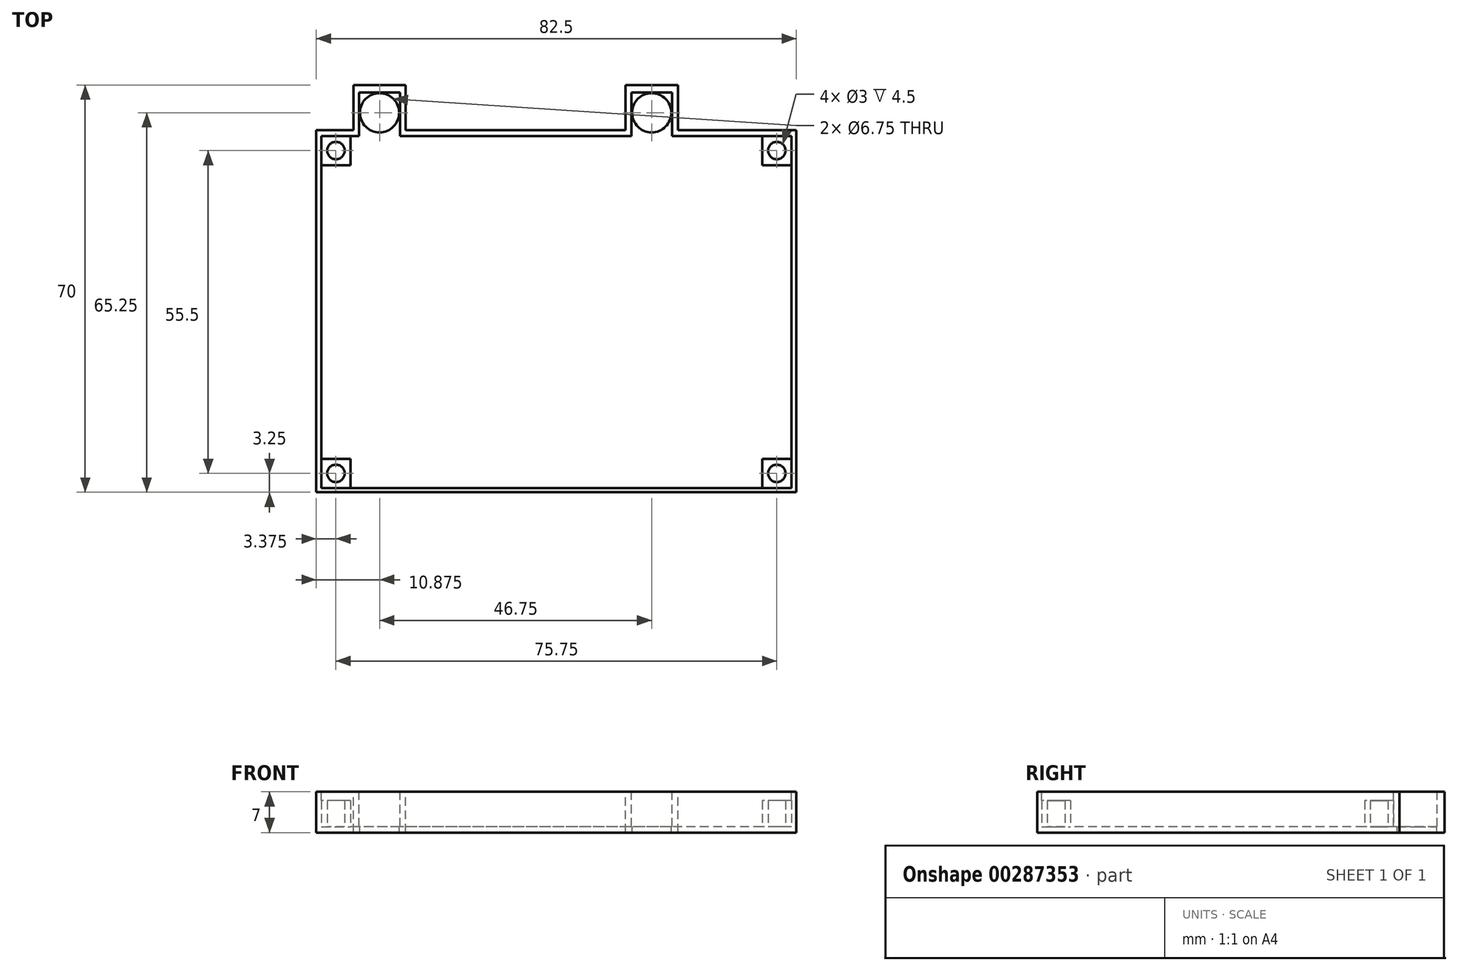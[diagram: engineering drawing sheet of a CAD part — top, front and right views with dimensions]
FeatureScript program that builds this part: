
annotation { "Feature Type Name" : "Feature", "Feature Type Description" : "" }
export const myFeature = defineFeature(function(context is Context, id is Id, definition is map)
    precondition{}
    {
        {
            var Q0;
            Q0=qCreatedBy(makeId("Top.planeOp"),FACE);
            var sketch = newSketch(context, id + "F0", { "sketchPlane" : qUnion([Q0])});
            skLineSegment(sketch, "E0.bottom", {"start": v(41.25, 35) * mm, "end": v(-41.25, 35) * mm});
            skLineSegment(sketch, "E0.top", {"start": v(41.25, -35) * mm, "end": v(-41.25, -35) * mm});
            skLineSegment(sketch, "E0.left", {"start": v(41.25, 35) * mm, "end": v(41.25, -35) * mm});
            skLineSegment(sketch, "E0.right", {"start": v(-41.25, 35) * mm, "end": v(-41.25, -35) * mm});
            skPoint(sketch, "E0.middle", {"position": v(0, 0) * mm});
            skSolve(sketch);
        }
        {
            var Q0;
            Q0=makeQuery(id+"F0.imprint","IMPRINT",FACE,{"disambiguationData":[TD([[makeQuery(id+"F0.imprint","IMPRINT",EDGE,{"derivedFrom":sQuery(id+"F0.wireOp",EDGE,"E0.bottom")}),1.0]])]});
            extrude(context, id + "F1", {"entities" : qUnion([Q0]), "depth" : 7 * mm});
        }
        {
            var Q0;
            Q0=makeQuery(id+"F1.opExtrude","CAP_FACE",FACE,{"disambiguationData":[OSD([sQuery(id+"F0.wireOp",EDGE,"E0.bottom"),sQuery(id+"F0.wireOp",EDGE,"E0.top"),sQuery(id+"F0.wireOp",EDGE,"E0.left"),sQuery(id+"F0.wireOp",EDGE,"E0.right")])],"isStart":false});
            var sketch = newSketch(context, id + "F2", { "sketchPlane" : qUnion([Q0])});
            skLineSegment(sketch, "E1.bottom", {"start": v(40.38, 26.25) * mm, "end": v(-40.38, 26.25) * mm});
            skLineSegment(sketch, "E1.top", {"start": v(40.38, -34.25) * mm, "end": v(-40.38, -34.25) * mm});
            skLineSegment(sketch, "E1.left", {"start": v(40.38, 26.25) * mm, "end": v(40.38, -34.25) * mm});
            skLineSegment(sketch, "E1.right", {"start": v(-40.38, 26.25) * mm, "end": v(-40.38, -34.25) * mm});
            skPoint(sketch, "E1.middle", {"position": v(0, -4) * mm});
            skLineSegment(sketch, "E2.bottom", {"start": v(-26.88, 33.75) * mm, "end": v(-33.88, 33.75) * mm});
            skLineSegment(sketch, "E2.top", {"start": v(-26.88, 26.25) * mm, "end": v(-33.88, 26.25) * mm});
            skLineSegment(sketch, "E2.left", {"start": v(-26.88, 33.75) * mm, "end": v(-26.88, 26.25) * mm});
            skLineSegment(sketch, "E2.right", {"start": v(-33.88, 33.75) * mm, "end": v(-33.88, 26.25) * mm});
            skPoint(sketch, "E2.middle", {"position": v(-30.38, 30) * mm});
            skLineSegment(sketch, "E3.bottom", {"start": v(19.87, 33.75) * mm, "end": v(12.87, 33.75) * mm});
            skLineSegment(sketch, "E3.top", {"start": v(19.87, 26.25) * mm, "end": v(12.87, 26.25) * mm});
            skLineSegment(sketch, "E3.left", {"start": v(19.87, 33.75) * mm, "end": v(19.87, 26.25) * mm});
            skLineSegment(sketch, "E3.right", {"start": v(12.87, 33.75) * mm, "end": v(12.87, 26.25) * mm});
            skPoint(sketch, "E3.middle", {"position": v(16.37, 30) * mm});
            skSolve(sketch);
        }
        {
            var Q0;
            Q0=makeQuery(id+"F2.imprint","IMPRINT",FACE,{"disambiguationData":[TD([[makeQuery(id+"F2.imprint","IMPRINT",EDGE,{"derivedFrom":sQuery(id+"F2.wireOp",EDGE,"E1.top")}),-1.0]])]});
            var Q1;
            Q1=makeQuery(id+"F2.imprint","IMPRINT",FACE,{"disambiguationData":[TD([[makeQuery(id+"F2.imprint","IMPRINT",EDGE,{"derivedFrom":sQuery(id+"F2.wireOp",EDGE,"E2.bottom")}),1.0]])]});
            var Q2;
            Q2=makeQuery(id+"F2.imprint","IMPRINT",FACE,{"disambiguationData":[TD([[makeQuery(id+"F2.imprint","IMPRINT",EDGE,{"derivedFrom":sQuery(id+"F2.wireOp",EDGE,"E3.bottom")}),1.0]])]});
            extrude(context, id + "F3", {"entities" : qUnion([Q0, Q1, Q2]), "operationType" : NewBodyOperationType.REMOVE, "oppositeDirection" : true, "depth" : 6 * mm});
        }
        {
            var Q0;
            Q0=makeQuery(id+"F3.boolean.opBoolean","COPY",FACE,{"derivedFrom":makeQuery(id+"F3.opExtrude","CAP_FACE",FACE,{"disambiguationData":[OSD([sQuery(id+"F2.wireOp",EDGE,"E1.bottom"),sQuery(id+"F2.wireOp",EDGE,"E1.top"),sQuery(id+"F2.wireOp",EDGE,"E1.left"),sQuery(id+"F2.wireOp",EDGE,"E1.right"),sQuery(id+"F2.wireOp",EDGE,"E2.bottom"),sQuery(id+"F2.wireOp",EDGE,"E2.left"),sQuery(id+"F2.wireOp",EDGE,"E2.right"),sQuery(id+"F2.wireOp",EDGE,"E3.bottom"),sQuery(id+"F2.wireOp",EDGE,"E3.left"),sQuery(id+"F2.wireOp",EDGE,"E3.right")])],"isStart":false})});
            var sketch = newSketch(context, id + "F4", { "sketchPlane" : qUnion([Q0])});
            skCircle(sketch, "E4", {"center": v(-30.38, 30.25) * mm, "radius": 3.5 * mm});
            skCircle(sketch, "E5", {"center": v(16.37, 30.25) * mm, "radius": 3.5 * mm});
            skCircle(sketch, "E6", {"center": v(16.37, 30.25) * mm, "radius": 3.38 * mm});
            skCircle(sketch, "E7", {"center": v(-30.38, 30.25) * mm, "radius": 3.38 * mm});
            skSolve(sketch);
        }
        {
            var Q0;
            Q0=makeQuery(id+"F4.imprint","IMPRINT",FACE,{"disambiguationData":[TD([[makeQuery(id+"F4.imprint","IMPRINT",EDGE,{"derivedFrom":sQuery(id+"F4.wireOp",EDGE,"E7")}),1.0]])]});
            var Q1;
            Q1=makeQuery(id+"F4.imprint","IMPRINT",FACE,{"disambiguationData":[TD([[makeQuery(id+"F4.imprint","IMPRINT",EDGE,{"derivedFrom":sQuery(id+"F4.wireOp",EDGE,"E6")}),1.0]])]});
            extrude(context, id + "F5", {"entities" : qUnion([Q0, Q1]), "operationType" : NewBodyOperationType.REMOVE, "oppositeDirection" : true, "depth" : 25 * mm});
        }
        {
            var Q0;
            Q0=makeQuery(id+"F3.boolean.opBoolean","COPY",FACE,{"derivedFrom":makeQuery(id+"F3.opExtrude","CAP_FACE",FACE,{"disambiguationData":[OSD([sQuery(id+"F2.wireOp",EDGE,"E1.bottom"),sQuery(id+"F2.wireOp",EDGE,"E1.top"),sQuery(id+"F2.wireOp",EDGE,"E1.left"),sQuery(id+"F2.wireOp",EDGE,"E1.right"),sQuery(id+"F2.wireOp",EDGE,"E2.bottom"),sQuery(id+"F2.wireOp",EDGE,"E2.left"),sQuery(id+"F2.wireOp",EDGE,"E2.right"),sQuery(id+"F2.wireOp",EDGE,"E3.bottom"),sQuery(id+"F2.wireOp",EDGE,"E3.left"),sQuery(id+"F2.wireOp",EDGE,"E3.right")])],"isStart":false})});
            var sketch = newSketch(context, id + "F6", { "sketchPlane" : qUnion([Q0])});
            skLineSegment(sketch, "E8.bottom", {"start": v(-40.38, 26.25) * mm, "end": v(-35.38, 26.25) * mm});
            skLineSegment(sketch, "E8.top", {"start": v(-40.38, 21.25) * mm, "end": v(-35.38, 21.25) * mm});
            skLineSegment(sketch, "E8.left", {"start": v(-40.38, 26.25) * mm, "end": v(-40.38, 21.25) * mm});
            skLineSegment(sketch, "E8.right", {"start": v(-35.38, 26.25) * mm, "end": v(-35.38, 21.25) * mm});
            skLineSegment(sketch, "E9.bottom", {"start": v(-40.38, -34.25) * mm, "end": v(-35.38, -34.25) * mm});
            skLineSegment(sketch, "E9.top", {"start": v(-40.38, -29.25) * mm, "end": v(-35.38, -29.25) * mm});
            skLineSegment(sketch, "E9.left", {"start": v(-40.38, -34.25) * mm, "end": v(-40.38, -29.25) * mm});
            skLineSegment(sketch, "E9.right", {"start": v(-35.38, -34.25) * mm, "end": v(-35.38, -29.25) * mm});
            skLineSegment(sketch, "E10.bottom", {"start": v(40.38, -34.25) * mm, "end": v(35.38, -34.25) * mm});
            skLineSegment(sketch, "E10.top", {"start": v(40.38, -29.25) * mm, "end": v(35.38, -29.25) * mm});
            skLineSegment(sketch, "E10.left", {"start": v(40.38, -34.25) * mm, "end": v(40.38, -29.25) * mm});
            skLineSegment(sketch, "E10.right", {"start": v(35.38, -34.25) * mm, "end": v(35.38, -29.25) * mm});
            skLineSegment(sketch, "E11.bottom", {"start": v(40.38, 26.25) * mm, "end": v(35.38, 26.25) * mm});
            skLineSegment(sketch, "E11.top", {"start": v(40.38, 21.25) * mm, "end": v(35.38, 21.25) * mm});
            skLineSegment(sketch, "E11.left", {"start": v(40.37, 26.25) * mm, "end": v(40.37, 21.25) * mm});
            skLineSegment(sketch, "E11.right", {"start": v(35.38, 26.25) * mm, "end": v(35.38, 21.25) * mm});
            skCircle(sketch, "E12", {"center": v(-37.88, 23.75) * mm, "radius": 1.5 * mm});
            skPoint(sketch, "E12.centerSnap0", {"position": v(-37.88, 21.25) * mm});
            skLineSegment(sketch, "E13", {"start": v(-35.38, 23.75) * mm, "end": v(-37.88, 23.75) * mm});
            skPoint(sketch, "E14.centerSnap0", {"position": v(-37.88, -29.25) * mm});
            skPoint(sketch, "E15.centerSnap0", {"position": v(37.88, -29.25) * mm});
            skCircle(sketch, "E16", {"center": v(37.88, 23.75) * mm, "radius": 1.5 * mm});
            skPoint(sketch, "E16.centerSnap0", {"position": v(35.38, 23.75) * mm});
            skPoint(sketch, "E16.centerSnap1", {"position": v(37.88, 21.25) * mm});
            skCircle(sketch, "E17", {"center": v(37.88, -31.75) * mm, "radius": 1.5 * mm});
            skPoint(sketch, "E17.centerSnap0", {"position": v(35.38, -31.75) * mm});
            skCircle(sketch, "E18", {"center": v(-37.88, -31.75) * mm, "radius": 1.5 * mm});
            skPoint(sketch, "E18.centerSnap0", {"position": v(-35.38, -31.75) * mm});
            skSolve(sketch);
        }
        {
            var Q0;
            Q0=makeQuery(id+"F6.imprint","IMPRINT",FACE,{"disambiguationData":[TD([[makeQuery(id+"F6.imprint","IMPRINT",EDGE,{"derivedFrom":sQuery(id+"F6.wireOp",EDGE,"E11.bottom")}),1.0]])]});
            var Q1;
            Q1=makeQuery(id+"F6.imprint","IMPRINT",FACE,{"disambiguationData":[TD([[makeQuery(id+"F6.imprint","IMPRINT",EDGE,{"derivedFrom":sQuery(id+"F6.wireOp",EDGE,"E10.bottom")}),-1.0]])]});
            var Q2;
            Q2=makeQuery(id+"F6.imprint","IMPRINT",FACE,{"disambiguationData":[TD([[makeQuery(id+"F6.imprint","IMPRINT",EDGE,{"derivedFrom":sQuery(id+"F6.wireOp",EDGE,"E9.bottom")}),-1.0]])]});
            var Q3;
            {var subQ1=sQuery(id+"F6.wireOp",EDGE,"E8.bottom");Q3=makeQuery(id+"F6.imprint","IMPRINT",FACE,{"disambiguationData":[TD([[makeQuery(id+"F6.imprint","IMPRINT",EDGE,{"derivedFrom":subQ1}),1.0]])]});}
            extrude(context, id + "F7", {"entities" : qUnion([Q0, Q1, Q2, Q3]), "operationType" : NewBodyOperationType.ADD, "depth" : 4.5 * mm});
        }
        {
            var Q0;
            Q0=makeQuery(id+"F1.opExtrude","CAP_FACE",FACE,{"disambiguationData":[OSD([sQuery(id+"F0.wireOp",EDGE,"E0.bottom"),sQuery(id+"F0.wireOp",EDGE,"E0.top"),sQuery(id+"F0.wireOp",EDGE,"E0.left"),sQuery(id+"F0.wireOp",EDGE,"E0.right")])],"isStart":false});
            var sketch = newSketch(context, id + "F8", { "sketchPlane" : qUnion([Q0])});
            skLineSegment(sketch, "E19.bottom", {"start": v(41.25, 35) * mm, "end": v(20.87, 35) * mm});
            skLineSegment(sketch, "E19.top", {"start": v(41.25, 27.25) * mm, "end": v(20.87, 27.25) * mm});
            skLineSegment(sketch, "E19.left", {"start": v(41.25, 35) * mm, "end": v(41.25, 27.25) * mm});
            skLineSegment(sketch, "E19.right", {"start": v(20.87, 35) * mm, "end": v(20.87, 27.25) * mm});
            skLineSegment(sketch, "E20.bottom", {"start": v(-41.25, 35) * mm, "end": v(-34.88, 35) * mm});
            skLineSegment(sketch, "E20.top", {"start": v(-41.25, 27.25) * mm, "end": v(-34.88, 27.25) * mm});
            skLineSegment(sketch, "E20.left", {"start": v(-41.25, 35) * mm, "end": v(-41.25, 27.25) * mm});
            skLineSegment(sketch, "E20.right", {"start": v(-34.88, 35) * mm, "end": v(-34.88, 27.25) * mm});
            skLineSegment(sketch, "E21.bottom", {"start": v(-25.88, 35) * mm, "end": v(11.87, 35) * mm});
            skLineSegment(sketch, "E21.top", {"start": v(-25.88, 27.25) * mm, "end": v(11.87, 27.25) * mm});
            skLineSegment(sketch, "E21.left", {"start": v(-25.88, 35) * mm, "end": v(-25.88, 27.25) * mm});
            skLineSegment(sketch, "E21.right", {"start": v(11.87, 35) * mm, "end": v(11.87, 27.25) * mm});
            skSolve(sketch);
        }
        {
            var Q0;
            Q0=makeQuery(id+"F8.imprint","IMPRINT",FACE,{"disambiguationData":[TD([[makeQuery(id+"F8.imprint","IMPRINT",EDGE,{"derivedFrom":sQuery(id+"F8.wireOp",EDGE,"E20.bottom")}),1.0]])]});
            var Q1;
            Q1=makeQuery(id+"F8.imprint","IMPRINT",FACE,{"disambiguationData":[TD([[makeQuery(id+"F8.imprint","IMPRINT",EDGE,{"derivedFrom":sQuery(id+"F8.wireOp",EDGE,"E21.bottom")}),1.0]])]});
            var Q2;
            Q2=makeQuery(id+"F8.imprint","IMPRINT",FACE,{"disambiguationData":[TD([[makeQuery(id+"F8.imprint","IMPRINT",EDGE,{"derivedFrom":sQuery(id+"F8.wireOp",EDGE,"E19.bottom")}),1.0]])]});
            extrude(context, id + "F9", {"entities" : qUnion([Q0, Q1, Q2]), "operationType" : NewBodyOperationType.REMOVE, "oppositeDirection" : true, "depth" : 25 * mm});
        }
    });
